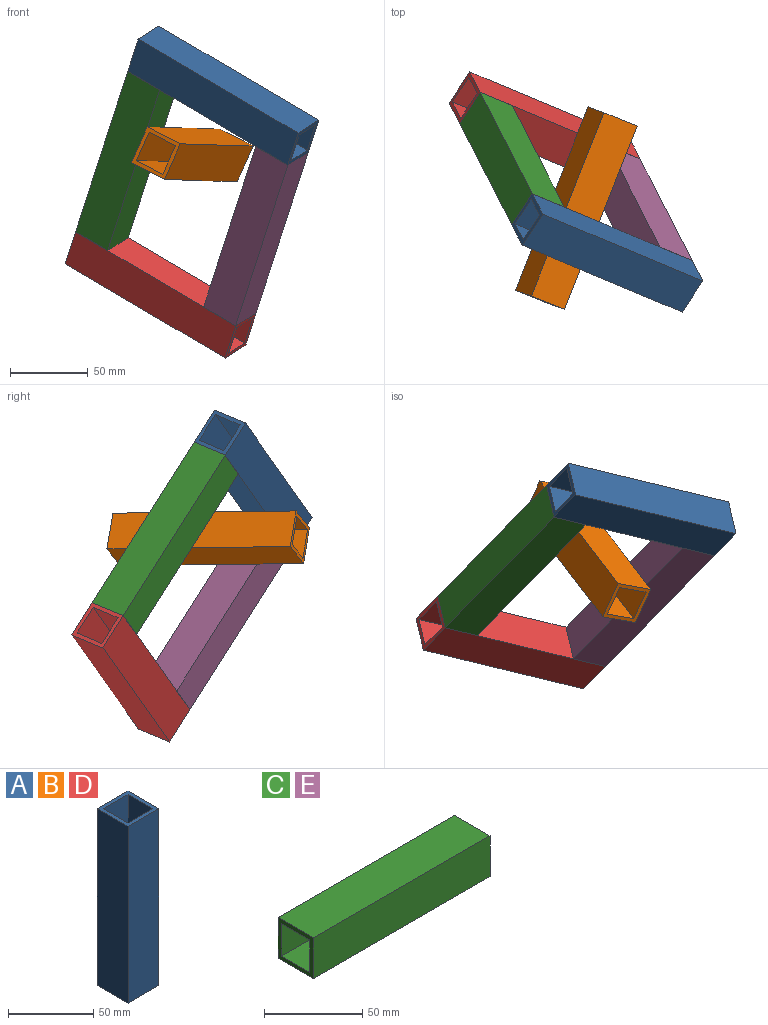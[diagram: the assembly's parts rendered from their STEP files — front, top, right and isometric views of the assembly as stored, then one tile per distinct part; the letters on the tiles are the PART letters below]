
ASSEMBLY  parts=5 mates=1
PART A: 10 faces, bbox 25.4x25.4x127 mm
  f0: plane 25.4x25.4mm, normal (0,0,1), area 232.3mm2, adj f2,f3,f4,f5,f6,f7,f8,f9
  f1: plane 25.4x25.4mm, normal (0,0,-1), area 232.3mm2, adj f2,f3,f4,f5,f6,f7,f8,f9
  f2: plane 127x25.4mm, normal (-1,0,0), area 3225.8mm2, adj f0,f1,f4,f5
  f3: plane 127x25.4mm, normal (1,0,0), area 3225.8mm2, adj f0,f1,f4,f5
  f4: plane 127x25.4mm, normal (0,-1,0), area 3225.8mm2, adj f0,f1,f2,f3
  f5: plane 127x25.4mm, normal (0,1,0), area 3225.8mm2, adj f0,f1,f2,f3
  f6: plane 127x20.32mm, normal (1,0,0), area 2580.6mm2, adj f0,f1,f8,f9
  f7: plane 127x20.32mm, normal (-1,0,0), area 2580.6mm2, adj f0,f1,f8,f9
  f8: plane 127x20.32mm, normal (0,1,0), area 2580.6mm2, adj f0,f1,f6,f7
  f9: plane 127x20.32mm, normal (0,-1,0), area 2580.6mm2, adj f0,f1,f6,f7
PART B: same geometry as A
PART C: 10 faces, bbox 127x25.4x25.4 mm
  f0: plane 25.4x25.4mm, normal (1,0,0), area 232.3mm2, adj f2,f3,f4,f5,f6,f7,f8,f9
  f1: plane 25.4x25.4mm, normal (-1,0,0), area 232.3mm2, adj f2,f3,f4,f5,f6,f7,f8,f9
  f2: plane 127x25.4mm, normal (0,0,-1), area 3225.8mm2, adj f0,f1,f4,f5
  f3: plane 127x25.4mm, normal (0,0,1), area 3225.8mm2, adj f0,f1,f4,f5
  f4: plane 127x25.4mm, normal (0,-1,0), area 3225.8mm2, adj f0,f1,f2,f3
  f5: plane 127x25.4mm, normal (0,1,0), area 3225.8mm2, adj f0,f1,f2,f3
  f6: plane 127x20.32mm, normal (0,0,1), area 2580.6mm2, adj f0,f1,f8,f9
  f7: plane 127x20.32mm, normal (0,0,-1), area 2580.6mm2, adj f0,f1,f8,f9
  f8: plane 127x20.32mm, normal (0,1,0), area 2580.6mm2, adj f0,f1,f6,f7
  f9: plane 127x20.32mm, normal (0,-1,0), area 2580.6mm2, adj f0,f1,f6,f7
PART D: same geometry as A
PART E: same geometry as C
PLACE A rot(axis=(0.38,0.93,0),118.5deg) t=(23.69,51.48,-28.75)mm
PLACE B rot(axis=(0.5,0.53,-0.69),149.8deg) t=(-7.24,28.64,-84.66)mm
PLACE C rot(axis=(0.38,0.93,0),118.5deg) t=(-47.73,67.75,45.57)mm
PLACE D rot(axis=(0.38,0.93,0),118.5deg) t=(-16.5,130.14,-152.94)mm
PLACE E rot(axis=(0.38,0.93,0),118.5deg) t=(34.69,33.36,-2.89)mm
MATE fastened A.f3 <-> C.f1  axis (-0.26,0.52,-0.81) through (-18.62,7.97,65.1)mm
